# Revit family: Faucet-Lavatory-KOHLER-Taut-K-74026T_1
name_source: partatom
category: Plumbing Fixtures
units: mm (PartAtom-declared; Revit-internal decimal feet)

## family parameters
Cut with Voids When Loaded = No
Host = Face
OmniClass Number = 23.31.11.00
OmniClass Title = Faucets
Part Type = Normal
Room Calculation Point = No
Round Connector Dimension = Use Diameter
Shared = No

## types (4) — shared parameters
ADA Compliant = No
Assembly Code = D2010
CW Connection = Yes
Cold Water Inlet = Cold Water Inlet
Date Modified = 11/17/2022
Default Elevation = 36"
Description = Single Control Tall Lavatory Faucet Without Drain
Drain Included = No
Flow Rate = 2 GPM
HW Connection = Yes
Handle Clearance = 3 1/8"
Height = 10 3/4"
Hot Water Inlet = Hot Water Inlet
Length = 4 3/4"
Manufacturer = Kohler Co.
Master Format 2014 = 22 41 39
Master Format 2014 Name = Residential Faucets, Supplies, and Trim
Material = Premium Metal Construction
Pressure = 43.51 psi
Product Name = Taut
Spout Reach = 4 3/4"
URL = http://www.kohler.com.cn
Vent Connection = No
Waste Connection = No
Waste Water Outlet = Waste Water Outlet
WaterSense Certified = No
Width = 2 3/16"

## per-type parameters (varying)
| type | 4ND | B4ND | Finish | Model | Secondary Material | Type |
| B4ND, CP-Polished Chrome | No | Yes | Kohler-Metal-CP-Polished_Chrome | K-74026T-B4ND-CP | Kohler-Plastic-58-Thunder_Grey | 1 |
| B4ND, BL-Matte Black | No | Yes | Kohler-Metal-BL-Matte_Black | K-74026T-B4ND-BL | Kohler-Plastic-7-Black_Black | 2 |
| 4ND, CP-Polished Chrome | Yes | No | Kohler-Metal-CP-Polished_Chrome | K-74026T-4ND-CP | Kohler-Plastic-58-Thunder_Grey | 3 |
| 4ND, BL-Matte Black | Yes | No | Kohler-Metal-BL-Matte_Black | K-74026T-4ND-BL | Kohler-Plastic-7-Black_Black | 4 |

## geometry (parser evidence)
native form markers: Sweep x4
no freeform markers — native parametric forms only
